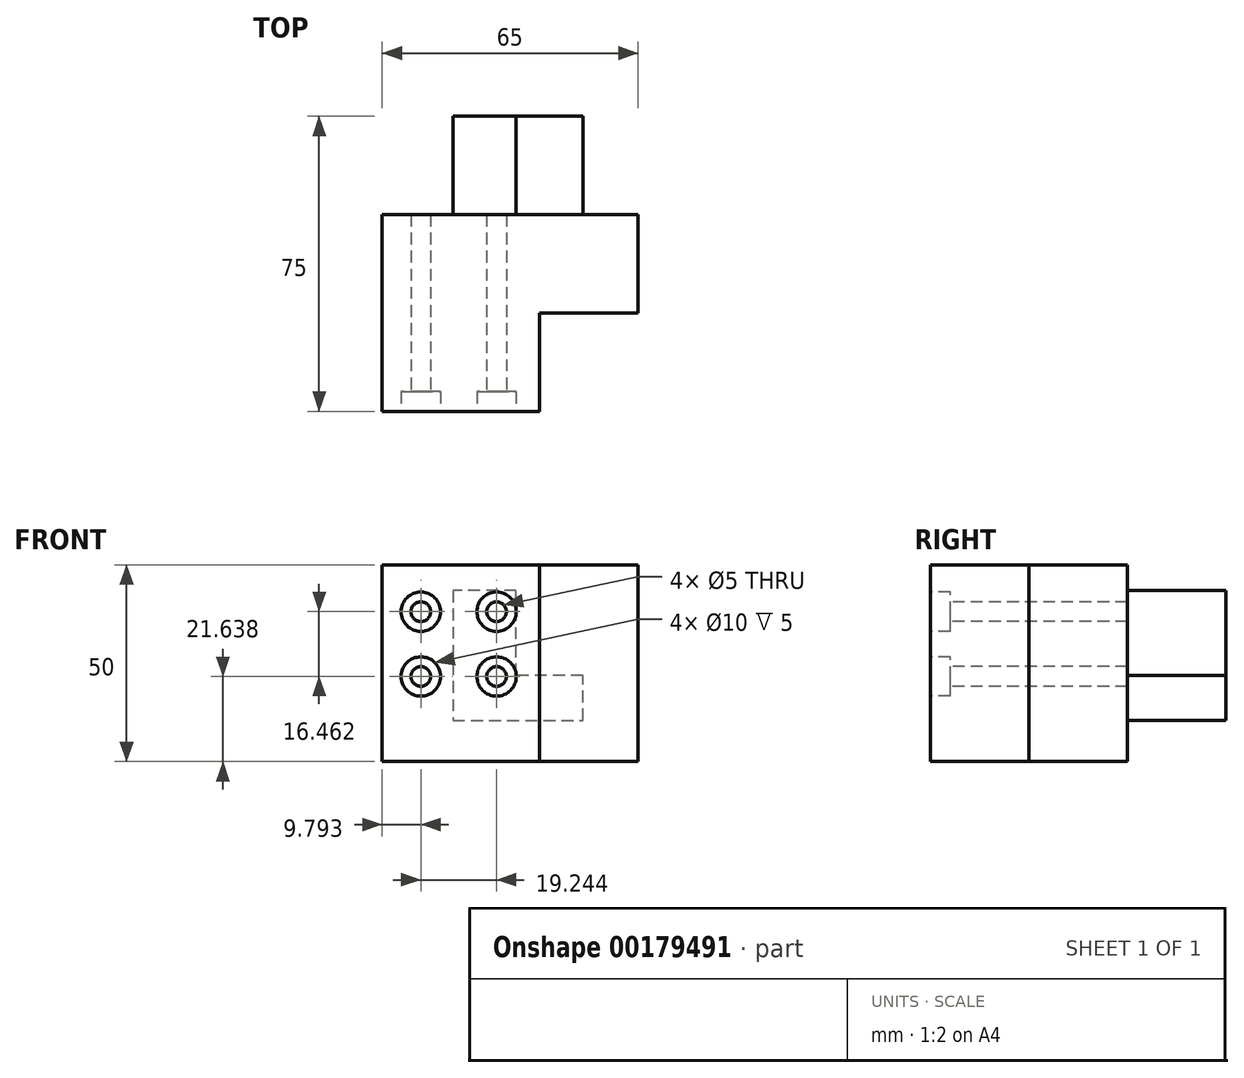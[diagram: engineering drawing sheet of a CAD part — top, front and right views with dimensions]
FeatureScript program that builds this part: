
annotation { "Feature Type Name" : "Feature", "Feature Type Description" : "" }
export const myFeature = defineFeature(function(context is Context, id is Id, definition is map)
    precondition{}
    {
        {
            var Q0;
            Q0=qCreatedBy(makeId("Top.planeOp"),FACE);
            var sketch = newSketch(context, id + "F4", { "sketchPlane" : qUnion([Q0])});
            skLineSegment(sketch, "E0", {"start": v(0, 0) * mm, "end": v(0, 50) * mm});
            skLineSegment(sketch, "E1", {"start": v(0, 50) * mm, "end": v(65, 50) * mm});
            skLineSegment(sketch, "E2", {"start": v(65, 50) * mm, "end": v(65, 25) * mm});
            skLineSegment(sketch, "E3", {"start": v(65, 25) * mm, "end": v(40, 25) * mm});
            skLineSegment(sketch, "E4", {"start": v(40, 25) * mm, "end": v(40, 0) * mm});
            skLineSegment(sketch, "E5", {"start": v(40, 0) * mm, "end": v(0, 0) * mm});
            skSolve(sketch);
        }
        {
            var Q0;
            Q0=makeQuery(id+"F4.imprint","IMPRINT",FACE,{"disambiguationData":[TD([[makeQuery(id+"F4.imprint","IMPRINT",EDGE,{"derivedFrom":sQuery(id+"F4.wireOp",EDGE,"E0")}),-1.0]])]});
            extrude(context, id + "F5", {"entities" : qUnion([Q0]), "depth" : 50 * mm});
        }
        {
            var Q0;
            Q0=makeQuery(id+"F5.opExtrude","SWEPT_FACE",FACE,{"disambiguationData":[OSD([sQuery(id+"F4.wireOp",EDGE,"E1")])]});
            var sketch = newSketch(context, id + "F0", { "sketchPlane" : qUnion([Q0])});
            skLineSegment(sketch, "E6", {"start": v(-17.96, 10.46) * mm, "end": v(-50.97, 10.46) * mm});
            skLineSegment(sketch, "E7", {"start": v(-50.97, 10.46) * mm, "end": v(-50.97, 21.92) * mm});
            skLineSegment(sketch, "E8", {"start": v(-50.97, 21.92) * mm, "end": v(-34.04, 21.92) * mm});
            skLineSegment(sketch, "E9", {"start": v(-34.04, 21.92) * mm, "end": v(-34.04, 43.47) * mm});
            skLineSegment(sketch, "E10", {"start": v(-34.04, 43.47) * mm, "end": v(-17.96, 43.47) * mm});
            skLineSegment(sketch, "E11", {"start": v(-17.96, 43.47) * mm, "end": v(-17.96, 10.46) * mm});
            skSolve(sketch);
        }
        {
            var Q0;
            Q0=makeQuery(id+"F5.opExtrude","SWEPT_FACE",FACE,{"disambiguationData":[OSD([sQuery(id+"F4.wireOp",EDGE,"E5")])]});
            var sketch = newSketch(context, id + "F1", { "sketchPlane" : qUnion([Q0])});
            skLineSegment(sketch, "E12.bottom", {"start": v(29.04, 38.1) * mm, "end": v(9.8, 38.1) * mm});
            skLineSegment(sketch, "E12.top", {"start": v(29.04, 21.64) * mm, "end": v(9.8, 21.64) * mm});
            skLineSegment(sketch, "E12.left", {"start": v(29.04, 38.1) * mm, "end": v(29.04, 21.64) * mm});
            skLineSegment(sketch, "E12.right", {"start": v(9.8, 38.1) * mm, "end": v(9.8, 21.64) * mm});
            skPoint(sketch, "E12.middle", {"position": v(19.41, 29.87) * mm});
            skSolve(sketch);
        }
        {
            var Q0;
            Q0=makeQuery(id+"F0.imprint","IMPRINT",FACE,{"disambiguationData":[TD([[makeQuery(id+"F0.imprint","IMPRINT",EDGE,{"derivedFrom":sQuery(id+"F0.wireOp",EDGE,"E6")}),-1.0]])]});
            extrude(context, id + "F2", {"entities" : qUnion([Q0]), "depth" : 25 * mm});
        }
        {
            var Q0;
            Q0=sQuery(id+"F1.wireOp",VERTEX,"E12.top.end");
            var Q1;
            Q1=sQuery(id+"F1.wireOp",VERTEX,"E12.left.end");
            var Q2;
            Q2=sQuery(id+"F1.wireOp",VERTEX,"E12.left.start");
            var Q3;
            Q3=sQuery(id+"F1.wireOp",VERTEX,"E12.bottom.end");
            var Q4;
            Q4=makeQuery(id+"F5.opExtrude","SWEPT_BODY",BODY,{"disambiguationData":[OSD([sQuery(id+"F4.wireOp",EDGE,"E0"),sQuery(id+"F4.wireOp",EDGE,"E1"),sQuery(id+"F4.wireOp",EDGE,"E2"),sQuery(id+"F4.wireOp",EDGE,"E3"),sQuery(id+"F4.wireOp",EDGE,"E4"),sQuery(id+"F4.wireOp",EDGE,"E5")])]});
            hole(context, id + "F3", {"style" : HoleStyle.C_BORE, "endStyle" : HoleEndStyle.THROUGH, "standardTappedOrClearance" : lookupTablePath({ "standard" : "ISO" }), "standardBlindInLast" : lookupTablePath({ "standard" : "ISO" }), "holeDiameter" : 5 * mm, "cBoreDiameter" : 10 * mm, "cBoreDepth" : 5 * mm, "startFromSketch" : true, "locations" : qUnion([Q0, Q1, Q2, Q3]), "scope" : qUnion([Q4]), "isTappedThrough" : true});
        }
    });
